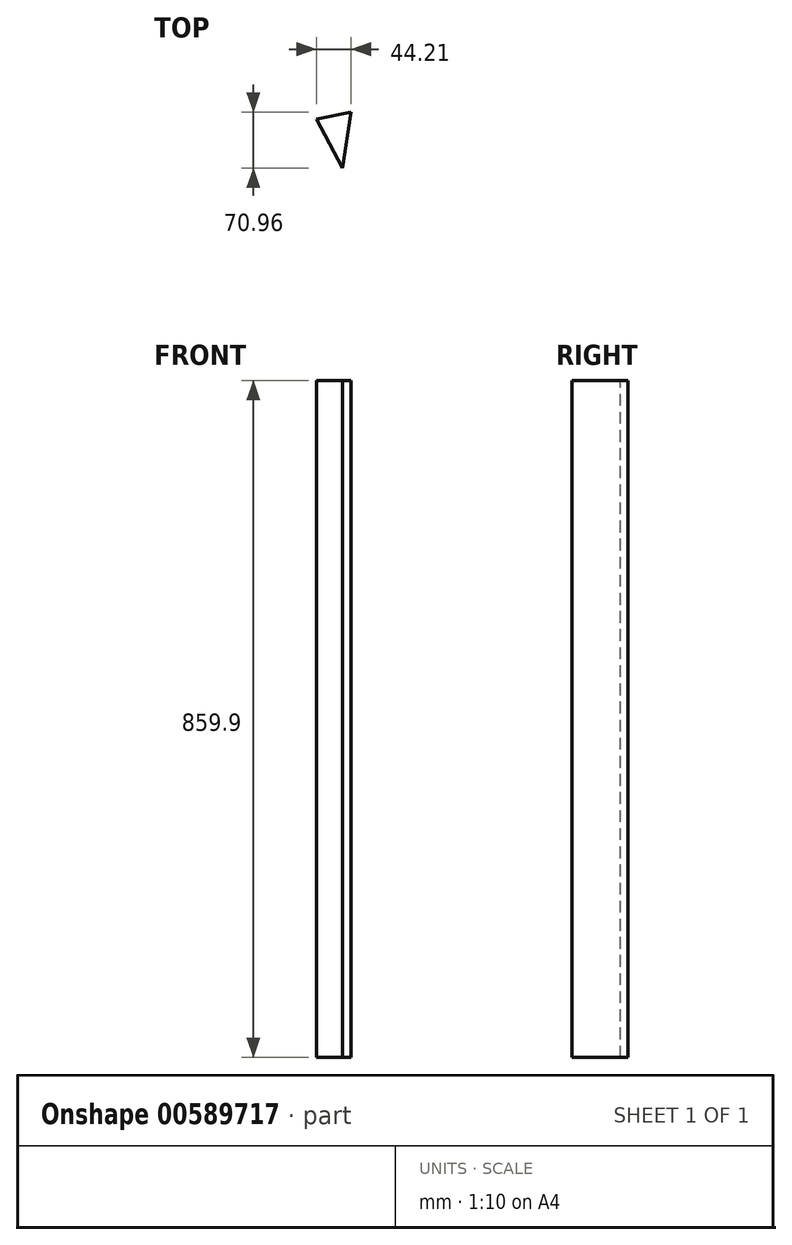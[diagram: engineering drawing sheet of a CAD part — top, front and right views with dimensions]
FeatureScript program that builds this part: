
annotation { "Feature Type Name" : "Feature", "Feature Type Description" : "" }
export const myFeature = defineFeature(function(context is Context, id is Id, definition is map)
    precondition{}
    {
        {
            var Q0;
            Q0=qCreatedBy(makeId("Top.planeOp"),FACE);
            var sketch = newSketch(context, id + "F0", { "sketchPlane" : qUnion([Q0])});
            skLineSegment(sketch, "E0", {"start": v(-70.36, 29) * mm, "end": v(-36.82, -32.83) * mm});
            skLineSegment(sketch, "E1", {"start": v(-36.82, -32.83) * mm, "end": v(-26.15, 38.13) * mm});
            skLineSegment(sketch, "E2", {"start": v(-26.15, 38.13) * mm, "end": v(-70.36, 29) * mm});
            skSolve(sketch);
        }
        {
            var Q0;
            Q0 = qSketchRegion(id + "F0", true);
            extrude(context, id + "F1", {"entities" : qUnion([Q0]), "oppositeDirection" : true, "depth" : 859.9 * mm, "offsetDistance" : 25.4 * mm});
        }
    });
